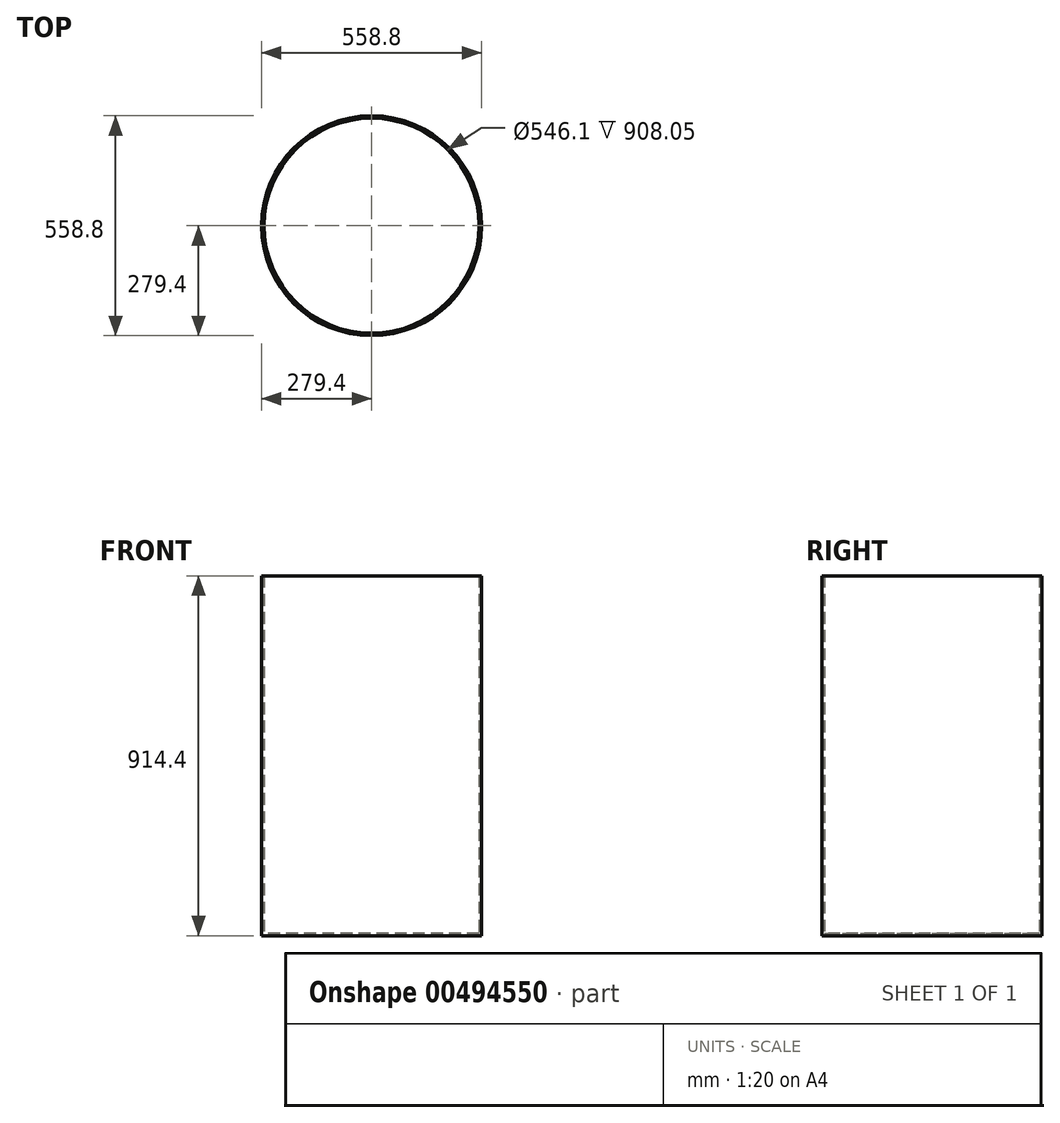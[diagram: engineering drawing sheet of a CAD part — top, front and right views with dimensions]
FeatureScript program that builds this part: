
annotation { "Feature Type Name" : "Feature", "Feature Type Description" : "" }
export const myFeature = defineFeature(function(context is Context, id is Id, definition is map)
    precondition{}
    {
        {
            var Q0;
            Q0=qCreatedBy(makeId("Top.planeOp"),FACE);
            var sketch = newSketch(context, id + "F0", { "sketchPlane" : qUnion([Q0])});
            skCircle(sketch, "E0", {"center": v(0, 0) * mm, "radius": 279.4 * mm});
            skSolve(sketch);
        }
        {
            var Q0;
            Q0 = qSketchRegion(id + "F0", true);
            extrude(context, id + "F1", {"entities" : qUnion([Q0]), "depth" : 914.4 * mm, "offsetDistance" : 25.4 * mm});
        }
        {
            var Q0;
            Q0=makeQuery(id+"F1.opExtrude","CAP_FACE",FACE,{"disambiguationData":[OSD([sQuery(id+"F0.wireOp",EDGE,"E0")])],"isStart":false});
            shell(context, id + "F2", {"entities" : qUnion([Q0]), "thickness" : 6.35 * mm});
        }
    });
